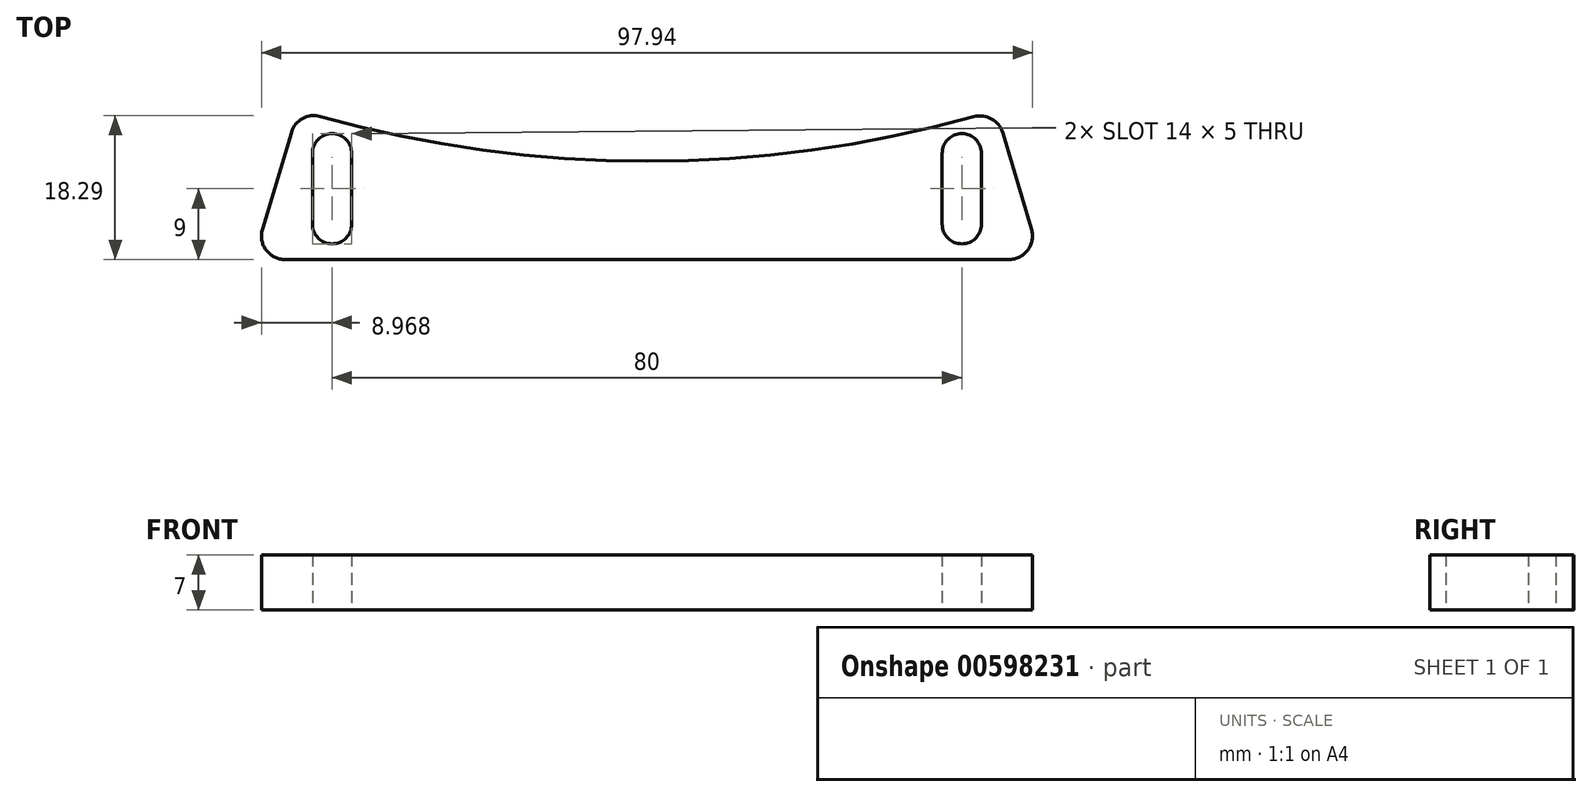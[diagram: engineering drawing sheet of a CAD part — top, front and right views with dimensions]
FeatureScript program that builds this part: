
annotation { "Feature Type Name" : "Feature", "Feature Type Description" : "" }
export const myFeature = defineFeature(function(context is Context, id is Id, definition is map)
    precondition{}
    {
        {
            var Q0;
            Q0=qCreatedBy(makeId("Top.planeOp"),FACE);
            var sketch = newSketch(context, id + "F0", { "sketchPlane" : qUnion([Q0])});
            skArc(sketch, "E0", {"start": v(-41.58, -149.32) * mm, "mid": v(-0.08, -155) * mm, "end": v(41.43, -149.36) * mm});
            skLineSegment(sketch, "E1.bottom", {"start": v(45.88, -167.5) * mm, "end": v(-46.06, -167.5) * mm});
            skPoint(sketch, "E2.orphan", {"position": v(-157.32, 167.5) * mm});
            skPoint(sketch, "E3.orphan", {"position": v(157.5, 167.5) * mm});
            skPoint(sketch, "E4.orphan", {"position": v(157.32, -167.5) * mm});
            skPoint(sketch, "E1.right.start.orphan", {"position": v(-157.5, -167.5) * mm});
            skArc(sketch, "E5", {"start": v(-42.6, -163) * mm, "mid": v(-40.1, -165.5) * mm, "end": v(-37.6, -163) * mm});
            skArc(sketch, "E6", {"start": v(37.4, -163) * mm, "mid": v(39.9, -165.5) * mm, "end": v(42.4, -163) * mm});
            skArc(sketch, "E7", {"start": v(-37.6, -154) * mm, "mid": v(-40.1, -151.5) * mm, "end": v(-42.6, -154) * mm});
            skArc(sketch, "E8", {"start": v(42.4, -154) * mm, "mid": v(39.9, -151.5) * mm, "end": v(37.4, -154) * mm});
            skLineSegment(sketch, "E9", {"start": v(45.1, -151.4) * mm, "end": v(48.76, -163.64) * mm});
            skLineSegment(sketch, "E10", {"start": v(-45.26, -151.35) * mm, "end": v(-48.94, -163.64) * mm});
            skLineSegment(sketch, "E11", {"start": v(-37.6, -154) * mm, "end": v(-37.6, -163) * mm});
            skLineSegment(sketch, "E12", {"start": v(-42.6, -154) * mm, "end": v(-42.6, -163) * mm});
            skLineSegment(sketch, "E13", {"start": v(37.4, -154) * mm, "end": v(37.4, -163) * mm});
            skLineSegment(sketch, "E14", {"start": v(42.4, -154) * mm, "end": v(42.4, -163) * mm});
            skPoint(sketch, "E15.visualSharp", {"position": v(-44.41, -148.5) * mm});
            skArc(sketch, "E15.filletArc", {"start": v(-41.58, -149.32) * mm, "mid": v(-43.84, -149.58) * mm, "end": v(-45.26, -151.35) * mm});
            skPoint(sketch, "E16.visualSharp", {"position": v(44.26, -148.55) * mm});
            skArc(sketch, "E16.filletArc", {"start": v(45.1, -151.4) * mm, "mid": v(43.69, -149.63) * mm, "end": v(41.43, -149.36) * mm});
            skPoint(sketch, "E17.visualSharp", {"position": v(49.9, -167.5) * mm});
            skArc(sketch, "E17.filletArc", {"start": v(45.88, -167.5) * mm, "mid": v(48.29, -166.3) * mm, "end": v(48.76, -163.64) * mm});
            skPoint(sketch, "E18.visualSharp", {"position": v(-50.1, -167.5) * mm});
            skArc(sketch, "E18.filletArc", {"start": v(-48.94, -163.64) * mm, "mid": v(-48.47, -166.3) * mm, "end": v(-46.06, -167.5) * mm});
            skPoint(sketch, "E19.trimOffspring.end.orphan", {"position": v(-0.1, -167.5) * mm});
            skPoint(sketch, "E20.trimOffspring.end.orphan", {"position": v(-0.08, -155) * mm});
            skSolve(sketch);
        }
        {
            var Q0;
            Q0=qSketchRegion(id+"F0",true);
            extrude(context, id + "F1", {"entities" : qUnion([Q0]), "depth" : 7 * mm, "offsetDistance" : 25 * mm});
        }
    });
